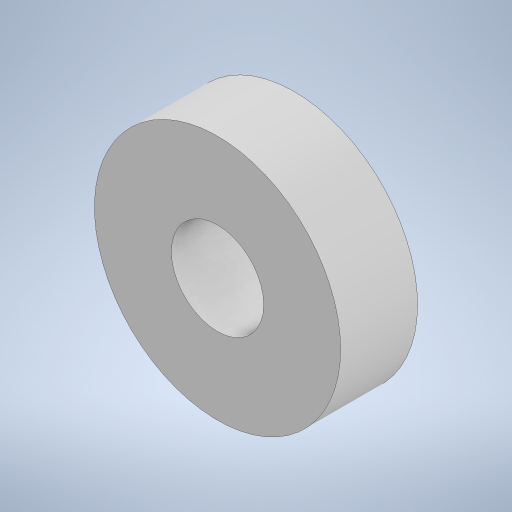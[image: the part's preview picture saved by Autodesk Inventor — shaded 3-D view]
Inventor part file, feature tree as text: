
AUTODESK INVENTOR PART (.ipt)
format: ipt  version: 2024 (Build 280153000, 153)  size: 211,456 bytes
history: native  units: mm
features: extrude x1, sketch x1
ambient origin geometry x8: Origin, YZ Plane, XZ Plane, XY Plane, X Axis, Y Axis, Z Axis, Center Point
bodies: Solid1 (feature_tree)
feature tree (2):
  extrude  "Extrusion1"  Depth=10.0mm
  sketch  "Sketch1"  dims[d0=32.0mm d1=12.0mm d2=10.0mm d3=0.0mm]
